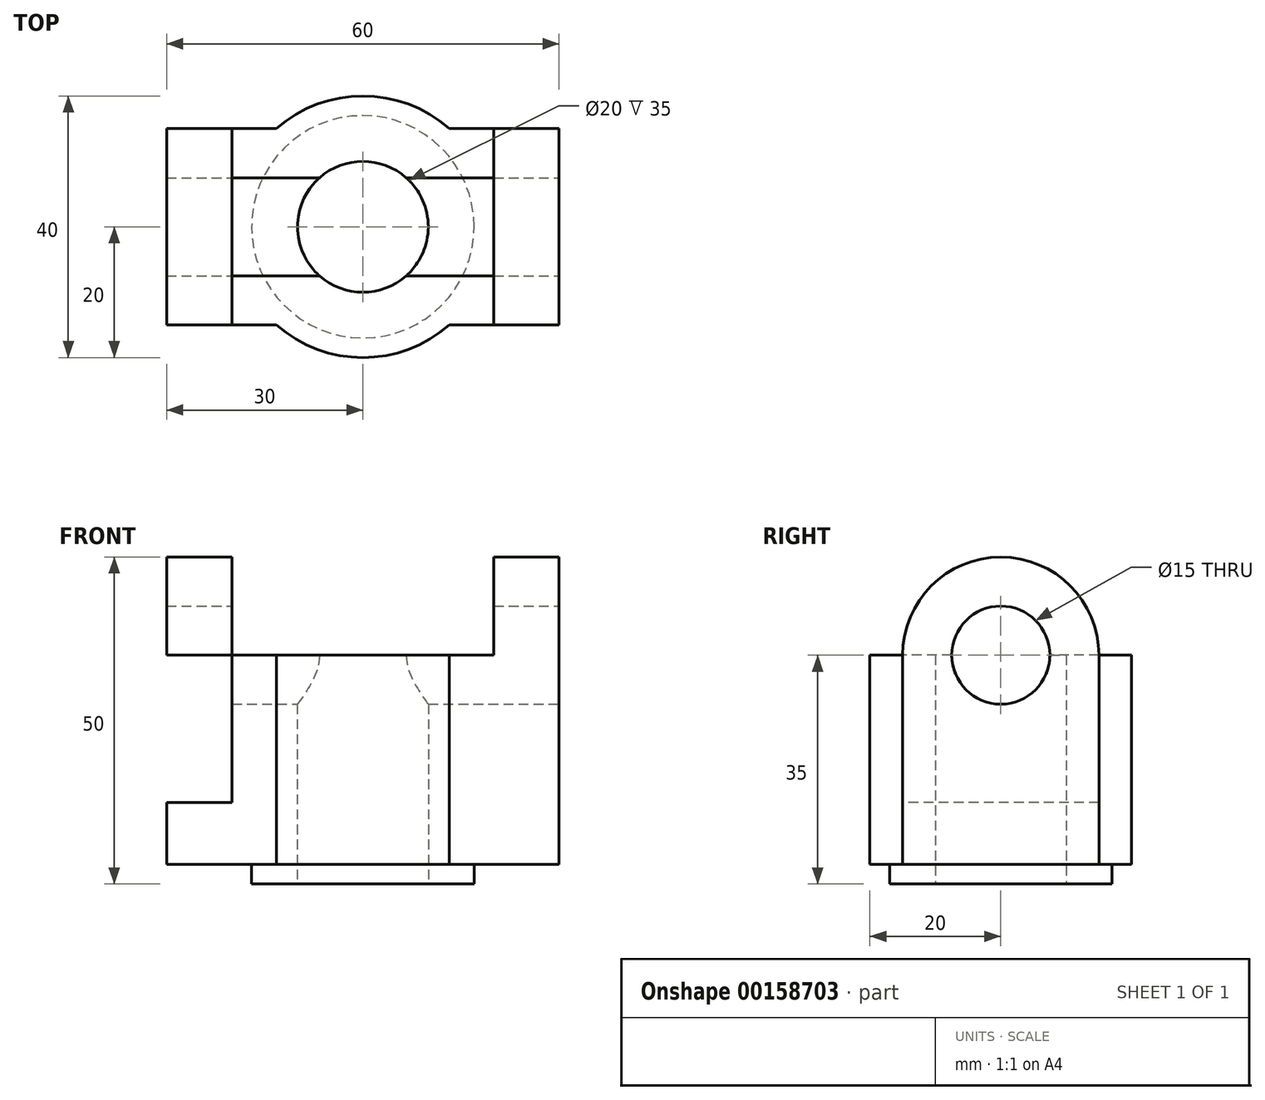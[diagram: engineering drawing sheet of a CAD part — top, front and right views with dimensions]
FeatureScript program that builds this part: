
annotation { "Feature Type Name" : "Feature", "Feature Type Description" : "" }
export const myFeature = defineFeature(function(context is Context, id is Id, definition is map)
    precondition{}
    {
        {
            var Q0;
            Q0=qCreatedBy(makeId("Top.planeOp"),FACE);
            var sketch = newSketch(context, id + "F0", { "sketchPlane" : qUnion([Q0])});
            skCircle(sketch, "E0", {"center": v(0, 0) * mm, "radius": 10 * mm});
            skArc(sketch, "E1", {"start": v(-13.23, -15) * mm, "mid": v(0, -20) * mm, "end": v(13.23, -15) * mm});
            skLineSegment(sketch, "E2.bottom", {"start": v(-30, 15) * mm, "end": v(-13.23, 15) * mm});
            skLineSegment(sketch, "E2.top", {"start": v(-30, -15) * mm, "end": v(-13.23, -15) * mm});
            skLineSegment(sketch, "E2.left", {"start": v(-30, 15) * mm, "end": v(-30, -15) * mm});
            skLineSegment(sketch, "E2.right", {"start": v(30, 15) * mm, "end": v(30, -15) * mm});
            skLineSegment(sketch, "E3", {"start": v(-37.3, 0) * mm, "end": v(47.87, 0) * mm, "construction": true});
            skLineSegment(sketch, "E4", {"start": v(0, 21.01) * mm, "end": v(0, -22.35) * mm, "construction": true});
            skLineSegment(sketch, "E5.trimOffspring", {"start": v(13.23, 15) * mm, "end": v(30, 15) * mm});
            skLineSegment(sketch, "E6.trimOffspring", {"start": v(13.23, -15) * mm, "end": v(30, -15) * mm});
            skArc(sketch, "E7.trimOffspring", {"start": v(13.23, 15) * mm, "mid": v(0, 20) * mm, "end": v(-13.23, 15) * mm});
            skSolve(sketch);
        }
        {
            var Q0;
            Q0=makeQuery(id+"F0.imprint","IMPRINT",FACE,{"disambiguationData":[TD([[makeQuery(id+"F0.imprint","IMPRINT",EDGE,{"derivedFrom":sQuery(id+"F0.wireOp",EDGE,"E0")}),-1.0]])]});
            extrude(context, id + "F1", {"entities" : qUnion([Q0]), "depth" : 32 * mm});
        }
        {
            var Q0;
            Q0=makeQuery(id+"F1.opExtrude","CAP_FACE",FACE,{"disambiguationData":[OSD([sQuery(id+"F0.wireOp",EDGE,"E0"),sQuery(id+"F0.wireOp",EDGE,"E1"),sQuery(id+"F0.wireOp",EDGE,"E2.bottom"),sQuery(id+"F0.wireOp",EDGE,"E2.top"),sQuery(id+"F0.wireOp",EDGE,"E2.left"),sQuery(id+"F0.wireOp",EDGE,"E2.right"),sQuery(id+"F0.wireOp",EDGE,"E5.trimOffspring"),sQuery(id+"F0.wireOp",EDGE,"E6.trimOffspring"),sQuery(id+"F0.wireOp",EDGE,"E7.trimOffspring")])],"isStart":false});
            var sketch = newSketch(context, id + "F2", { "sketchPlane" : qUnion([Q0])});
            skLineSegment(sketch, "E8.0", {"start": v(-30, 15) * mm, "end": v(-30, -15) * mm});
            skLineSegment(sketch, "E9.0", {"start": v(-30, 15) * mm, "end": v(-13.23, 15) * mm});
            skLineSegment(sketch, "E10.0", {"start": v(-30, -15) * mm, "end": v(-13.23, -15) * mm});
            skLineSegment(sketch, "E11.0", {"start": v(13.23, -15) * mm, "end": v(30, -15) * mm});
            skLineSegment(sketch, "E12.0", {"start": v(30, 15) * mm, "end": v(30, -15) * mm});
            skLineSegment(sketch, "E13.0", {"start": v(13.23, 15) * mm, "end": v(30, 15) * mm});
            skLineSegment(sketch, "E14.bottom", {"start": v(-30, 15) * mm, "end": v(-20, 15) * mm});
            skLineSegment(sketch, "E14.top", {"start": v(-30, -15) * mm, "end": v(-20, -15) * mm});
            skLineSegment(sketch, "E14.right", {"start": v(-20, 15) * mm, "end": v(-20, -15) * mm});
            skLineSegment(sketch, "E15.bottom", {"start": v(30, 15) * mm, "end": v(20, 15) * mm});
            skLineSegment(sketch, "E15.top", {"start": v(30, -15) * mm, "end": v(20, -15) * mm});
            skLineSegment(sketch, "E15.right", {"start": v(20, 15) * mm, "end": v(20, -15) * mm});
            skSolve(sketch);
        }
        {
            var Q0;
            Q0=makeQuery(id+"F2.imprint","IMPRINT",FACE,{"disambiguationData":[TD([[makeQuery(id+"F2.imprint","IMPRINT",EDGE,{"derivedFrom":sQuery(id+"F2.wireOp",EDGE,"E9.0")}),-1.0]])]});
            extrude(context, id + "F3", {"entities" : qUnion([Q0]), "operationType" : NewBodyOperationType.REMOVE, "oppositeDirection" : true, "depth" : 22.5 * mm});
        }
        {
            var Q0;
            Q0=makeQuery(id+"F1.opExtrude","CAP_FACE",FACE,{"disambiguationData":[OSD([sQuery(id+"F0.wireOp",EDGE,"E0"),sQuery(id+"F0.wireOp",EDGE,"E1"),sQuery(id+"F0.wireOp",EDGE,"E2.bottom"),sQuery(id+"F0.wireOp",EDGE,"E2.top"),sQuery(id+"F0.wireOp",EDGE,"E2.left"),sQuery(id+"F0.wireOp",EDGE,"E2.right"),sQuery(id+"F0.wireOp",EDGE,"E5.trimOffspring"),sQuery(id+"F0.wireOp",EDGE,"E6.trimOffspring"),sQuery(id+"F0.wireOp",EDGE,"E7.trimOffspring")])],"isStart":true});
            var sketch = newSketch(context, id + "F4", { "sketchPlane" : qUnion([Q0])});
            skCircle(sketch, "E16", {"center": v(0, 0) * mm, "radius": 17 * mm});
            skCircle(sketch, "E17", {"center": v(0, 0) * mm, "radius": 10 * mm});
            skSolve(sketch);
        }
        {
            var Q0;
            Q0 = qSketchRegion(id + "F4", true);
            extrude(context, id + "F5", {"entities" : qUnion([Q0]), "operationType" : NewBodyOperationType.ADD, "depth" : 3 * mm});
        }
        {
            var Q0;
            Q0=makeQuery(id+"F1.opExtrude","SWEPT_FACE",FACE,{"disambiguationData":[OSD([sQuery(id+"F0.wireOp",EDGE,"E2.right")])]});
            var sketch = newSketch(context, id + "F6", { "sketchPlane" : qUnion([Q0])});
            skLineSegment(sketch, "E18.0", {"start": v(15, 32) * mm, "end": v(-15, 32) * mm});
            skCircle(sketch, "E19", {"center": v(0, 32) * mm, "radius": 7.5 * mm});
            skArc(sketch, "E20", {"start": v(15, 32) * mm, "mid": v(0, 47) * mm, "end": v(-15, 32) * mm});
            skSolve(sketch);
        }
        {
            var Q0;
            {var subQ0=sQuery(id+"F6.wireOp",EDGE,"E20");Q0=makeQuery(id+"F6.imprint","IMPRINT",FACE,{"disambiguationData":[TD([[makeQuery(id+"F6.imprint","IMPRINT",EDGE,{"derivedFrom":subQ0}),1.0]])]});}
            extrude(context, id + "F7", {"entities" : qUnion([Q0]), "operationType" : NewBodyOperationType.ADD, "oppositeDirection" : true, "depth" : 60 * mm});
        }
        {
            var Q0;
            {var subQ0=sQuery(id+"F6.wireOp",EDGE,"E19");var subQ1=sQuery(id+"F6.wireOp",EDGE,"E18.0");var subQ2=makeQuery(id+"F6.imprint","INTERSECT",VERTEX,{"disambiguationData":[OD(0.0)],"derivedFrom":[subQ1,subQ0]});Q0=makeQuery(id+"F6.imprint","IMPRINT",FACE,{"disambiguationData":[TD([[makeQuery(id+"F6.imprint","IMPRINT",EDGE,{"disambiguationData":[TD([[subQ2,-1.0]])],"derivedFrom":subQ1}),1.0]])]});}
            extrude(context, id + "F8", {"entities" : qUnion([Q0]), "operationType" : NewBodyOperationType.REMOVE, "oppositeDirection" : true, "depth" : 60 * mm});
        }
        {
            var Q0;
            Q0=qCreatedBy(makeId("Front.planeOp"),FACE);
            var sketch = newSketch(context, id + "F9", { "sketchPlane" : qUnion([Q0])});
            skLineSegment(sketch, "E21.0", {"start": v(-20, 32) * mm, "end": v(20, 32) * mm});
            skLineSegment(sketch, "E22.top", {"start": v(-20, 51.35) * mm, "end": v(20, 51.35) * mm});
            skLineSegment(sketch, "E22.left", {"start": v(-20, 32) * mm, "end": v(-20, 51.35) * mm});
            skLineSegment(sketch, "E22.right", {"start": v(20, 32) * mm, "end": v(20, 51.35) * mm});
            skSolve(sketch);
        }
        {
            var Q0;
            Q0 = qSketchRegion(id + "F9", true);
            extrude(context, id + "F10", {"entities" : qUnion([Q0]), "operationType" : NewBodyOperationType.REMOVE, "oppositeDirection" : true, "depth" : 25 * mm, "hasSecondDirection" : true, "secondDirectionOppositeDirection" : false, "secondDirectionDepth" : 25 * mm});
        }
    });
